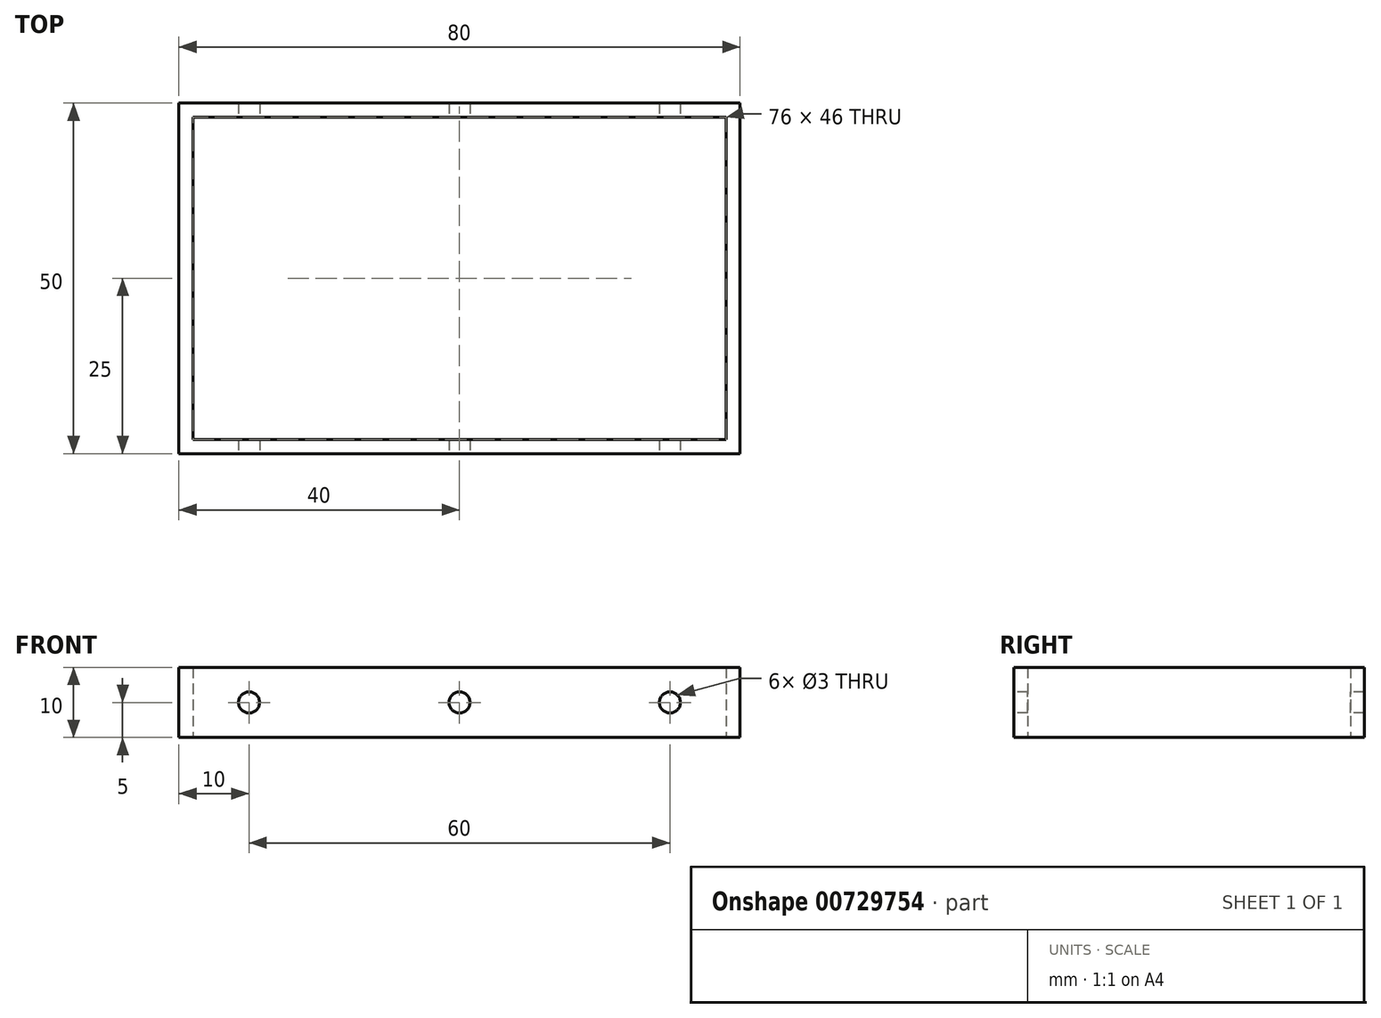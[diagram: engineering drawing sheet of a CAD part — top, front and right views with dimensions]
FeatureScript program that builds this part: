
annotation { "Feature Type Name" : "Feature", "Feature Type Description" : "" }
export const myFeature = defineFeature(function(context is Context, id is Id, definition is map)
    precondition{}
    {
        {
            var Q0;
            Q0=qCreatedBy(makeId("Top.planeOp"),FACE);
            var sketch = newSketch(context, id + "F0", { "sketchPlane" : qUnion([Q0])});
            skLineSegment(sketch, "E0.bottom", {"start": v(40, -25) * mm, "end": v(-40, -25) * mm});
            skLineSegment(sketch, "E0.top", {"start": v(40, 25) * mm, "end": v(-40, 25) * mm});
            skLineSegment(sketch, "E0.left", {"start": v(40, -25) * mm, "end": v(40, 25) * mm});
            skLineSegment(sketch, "E0.right", {"start": v(-40, -25) * mm, "end": v(-40, 25) * mm});
            skPoint(sketch, "E0.middle", {"position": v(0, 0) * mm});
            skSolve(sketch);
        }
        {
            var Q0;
            Q0=makeQuery(id+"F0.imprint","IMPRINT",FACE,{"disambiguationData":[TD([[makeQuery(id+"F0.imprint","IMPRINT",EDGE,{"derivedFrom":sQuery(id+"F0.wireOp",EDGE,"E0.bottom")}),-1.0]])]});
            extrude(context, id + "F1", {"entities" : qUnion([Q0]), "depth" : 10 * mm, "offsetDistance" : 25 * mm});
        }
        {
            var Q0;
            Q0=makeQuery(id+"F1.opExtrude","CAP_FACE",FACE,{"disambiguationData":[OSD([sQuery(id+"F0.wireOp",EDGE,"E0.bottom"),sQuery(id+"F0.wireOp",EDGE,"E0.top"),sQuery(id+"F0.wireOp",EDGE,"E0.left"),sQuery(id+"F0.wireOp",EDGE,"E0.right")])],"isStart":false});
            var Q1;
            Q1=makeQuery(id+"F1.opExtrude","CAP_FACE",FACE,{"disambiguationData":[OSD([sQuery(id+"F0.wireOp",EDGE,"E0.bottom"),sQuery(id+"F0.wireOp",EDGE,"E0.top"),sQuery(id+"F0.wireOp",EDGE,"E0.left"),sQuery(id+"F0.wireOp",EDGE,"E0.right")])],"isStart":true});
            shell(context, id + "F2", {"entities" : qUnion([Q0, Q1]), "thickness" : 2 * mm});
        }
        {
            var Q0;
            Q0=qCreatedBy(makeId("Front.planeOp"),FACE);
            var sketch = newSketch(context, id + "F3", { "sketchPlane" : qUnion([Q0])});
            skCircle(sketch, "E1", {"center": v(0, 5) * mm, "radius": 1.5 * mm});
            skCircle(sketch, "E2", {"center": v(30, 5) * mm, "radius": 1.5 * mm});
            skCircle(sketch, "E3", {"center": v(-30, 5) * mm, "radius": 1.5 * mm});
            skSolve(sketch);
        }
        {
            var Q0;
            Q0 = qSketchRegion(id + "F3", true);
            extrude(context, id + "F4", {"entities" : qUnion([Q0]), "operationType" : NewBodyOperationType.REMOVE, "endBound" : BoundingType.SYMMETRIC, "oppositeDirection" : true, "depth" : 50 * mm, "offsetDistance" : 25 * mm});
        }
    });
